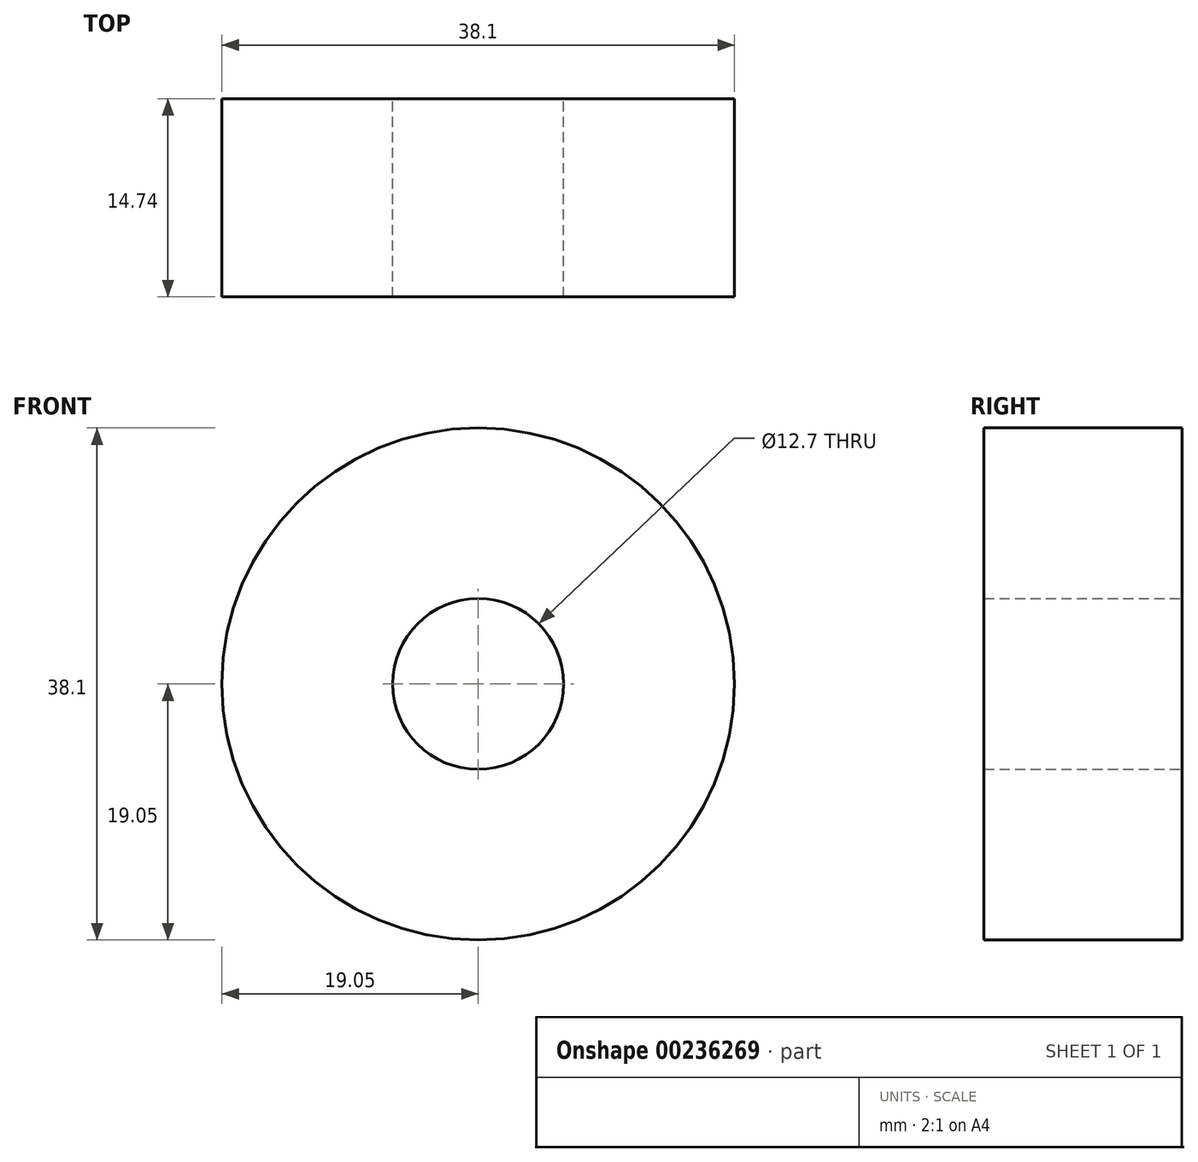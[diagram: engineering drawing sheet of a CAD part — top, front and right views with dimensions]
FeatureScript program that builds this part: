
annotation { "Feature Type Name" : "Feature", "Feature Type Description" : "" }
export const myFeature = defineFeature(function(context is Context, id is Id, definition is map)
    precondition{}
    {
        {
            var Q0;
            Q0=qCreatedBy(makeId("Front.planeOp"),FACE);
            var sketch = newSketch(context, id + "F0", { "sketchPlane" : qUnion([Q0])});
            skCircle(sketch, "E0", {"center": v(0, 0) * mm, "radius": 6.35 * mm});
            skCircle(sketch, "E1", {"center": v(0, 0) * mm, "radius": 19.05 * mm});
            skSolve(sketch);
        }
        {
            var Q0;
            Q0 = qSketchRegion(id + "F0", true);
            extrude(context, id + "F1", {"entities" : qUnion([Q0]), "endBound" : BoundingType.SYMMETRIC, "depth" : 14.73 * mm});
        }
    });
